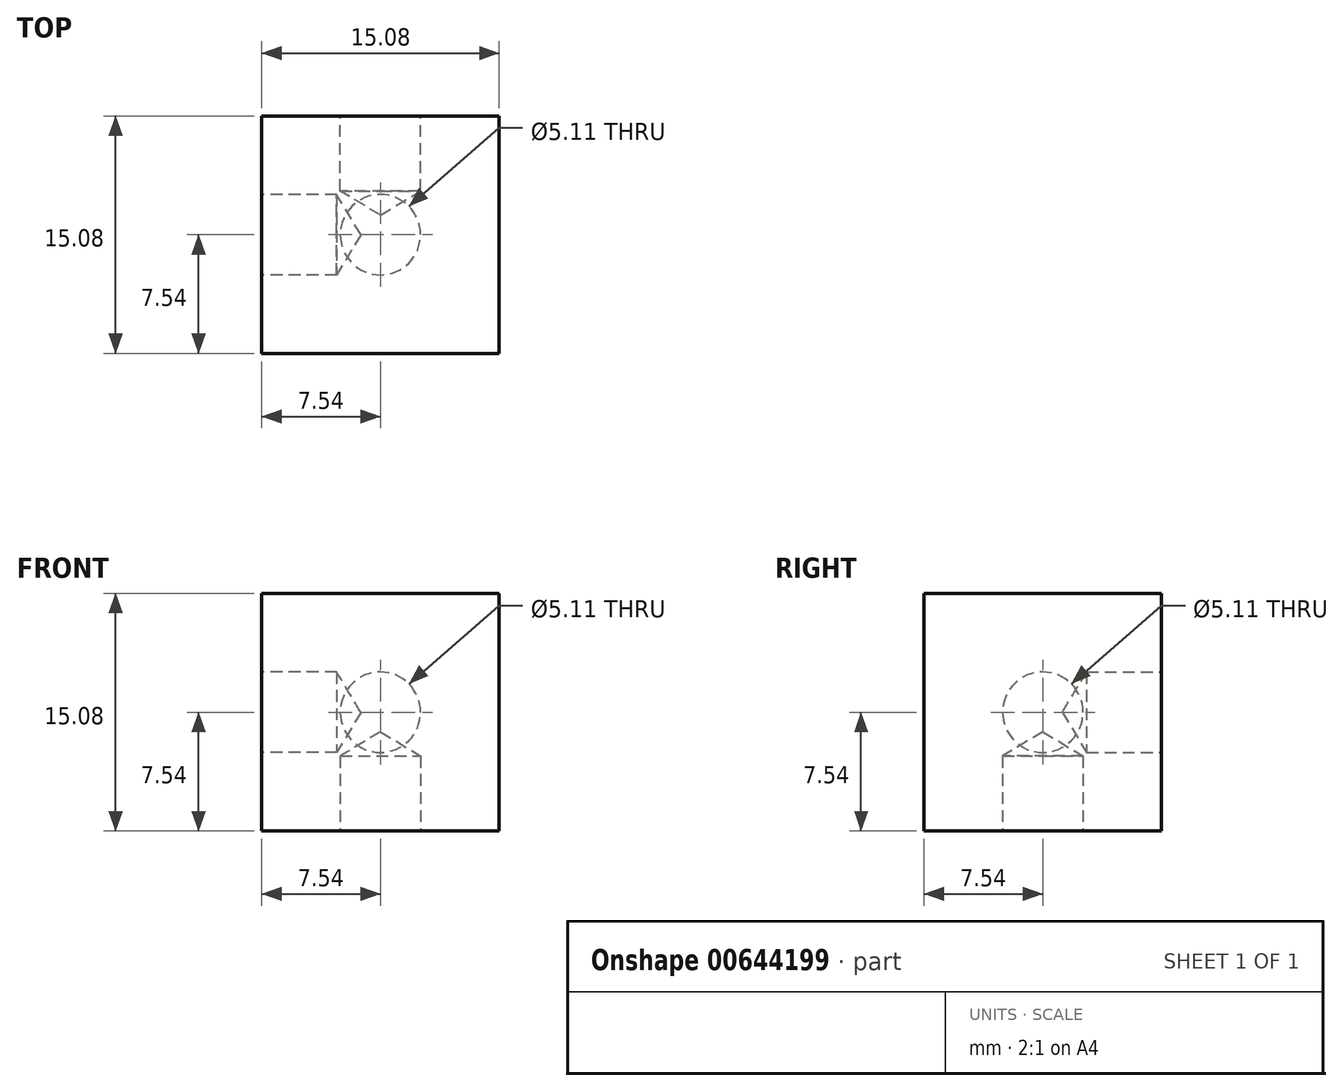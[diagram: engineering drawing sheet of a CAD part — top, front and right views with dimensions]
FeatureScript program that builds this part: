
annotation { "Feature Type Name" : "Feature", "Feature Type Description" : "" }
export const myFeature = defineFeature(function(context is Context, id is Id, definition is map)
    precondition{}
    {
        {
            var Q0;
            Q0=qCreatedBy(makeId("Top.planeOp"),FACE);
            var sketch = newSketch(context, id + "F0", { "sketchPlane" : qUnion([Q0])});
            skLineSegment(sketch, "E0.bottom", {"start": v(7.54, 7.54) * mm, "end": v(-7.54, 7.54) * mm});
            skLineSegment(sketch, "E0.top", {"start": v(7.54, -7.54) * mm, "end": v(-7.54, -7.54) * mm});
            skLineSegment(sketch, "E0.left", {"start": v(7.54, 7.54) * mm, "end": v(7.54, -7.54) * mm});
            skLineSegment(sketch, "E0.right", {"start": v(-7.54, 7.54) * mm, "end": v(-7.54, -7.54) * mm});
            skPoint(sketch, "E0.middle", {"position": v(0, 0) * mm});
            skSolve(sketch);
        }
        {
            var Q0;
            Q0=makeQuery(id+"F0.imprint","IMPRINT",FACE,{"disambiguationData":[TD([[makeQuery(id+"F0.imprint","IMPRINT",EDGE,{"derivedFrom":sQuery(id+"F0.wireOp",EDGE,"E0.bottom")}),1.0]])]});
            extrude(context, id + "F1", {"entities" : qUnion([Q0]), "endBound" : BoundingType.SYMMETRIC, "depth" : 15.08 * mm, "offsetDistance" : 25.4 * mm});
        }
        {
            var Q0;
            Q0=makeQuery(id+"F1.opExtrude","SWEPT_FACE",FACE,{"disambiguationData":[OSD([sQuery(id+"F0.wireOp",EDGE,"E0.right")])]});
            var sketch = newSketch(context, id + "F2", { "sketchPlane" : qUnion([Q0])});
            skPoint(sketch, "E1", {"position": v(0, 0) * mm});
            skSolve(sketch);
        }
        {
            var Q0;
            Q0=makeQuery(id+"F1.opExtrude","SWEPT_FACE",FACE,{"disambiguationData":[OSD([sQuery(id+"F0.wireOp",EDGE,"E0.bottom")])]});
            var sketch = newSketch(context, id + "F3", { "sketchPlane" : qUnion([Q0])});
            skPoint(sketch, "E2", {"position": v(0, 0) * mm});
            skSolve(sketch);
        }
        {
            var Q0;
            Q0=makeQuery(id+"F1.opExtrude","CAP_FACE",FACE,{"disambiguationData":[OSD([sQuery(id+"F0.wireOp",EDGE,"E0.bottom"),sQuery(id+"F0.wireOp",EDGE,"E0.top"),sQuery(id+"F0.wireOp",EDGE,"E0.left"),sQuery(id+"F0.wireOp",EDGE,"E0.right")])],"isStart":true});
            var sketch = newSketch(context, id + "F4", { "sketchPlane" : qUnion([Q0])});
            skPoint(sketch, "E3", {"position": v(0, 0) * mm});
            skSolve(sketch);
        }
        {
            var Q0;
            Q0=sQuery(id+"F4.wireOp",VERTEX,"E3");
            var Q1;
            Q1=makeQuery(id+"F1.opExtrude","SWEPT_BODY",BODY,{"disambiguationData":[OSD([sQuery(id+"F0.wireOp",EDGE,"E0.bottom"),sQuery(id+"F0.wireOp",EDGE,"E0.top"),sQuery(id+"F0.wireOp",EDGE,"E0.left"),sQuery(id+"F0.wireOp",EDGE,"E0.right")])]});
            hole(context, id + "F5", {"style" : HoleStyle.SIMPLE, "endStyle" : HoleEndStyle.BLIND, "standardTappedOrClearance" : lookupTablePath({ "standard" : "ANSI", "fit" : "Normal (ASME)", "size" : "#10", "type" : "Clearance" }), "standardBlindInLast" : lookupTablePath({ "fit" : "Free", "standard" : "ANSI", "size" : "#10", "type" : "Clearance" }), "holeDiameter" : 5.1 * mm, "majorDiameter" : 4.83 * mm, "holeDepth" : 4.76 * mm, "isTappedThrough" : true, "tappedDepth" : 12.7 * mm, "tapClearance" : 3, "locations" : qUnion([Q0]), "scope" : qUnion([Q1])});
        }
        {
            var Q0;
            Q0=sQuery(id+"F3.wireOp",VERTEX,"E2");
            var Q1;
            Q1=makeQuery(id+"F1.opExtrude","SWEPT_BODY",BODY,{"disambiguationData":[OSD([sQuery(id+"F0.wireOp",EDGE,"E0.bottom"),sQuery(id+"F0.wireOp",EDGE,"E0.top"),sQuery(id+"F0.wireOp",EDGE,"E0.left"),sQuery(id+"F0.wireOp",EDGE,"E0.right")])]});
            hole(context, id + "F6", {"style" : HoleStyle.SIMPLE, "endStyle" : HoleEndStyle.BLIND, "standardTappedOrClearance" : lookupTablePath({ "standard" : "ANSI", "fit" : "Normal (ASME)", "size" : "#10", "type" : "Clearance" }), "standardBlindInLast" : lookupTablePath({ "fit" : "Free", "standard" : "ANSI", "size" : "#10", "type" : "Clearance" }), "holeDiameter" : 5.1 * mm, "majorDiameter" : 6.35 * mm, "holeDepth" : 4.76 * mm, "isTappedThrough" : true, "tappedDepth" : 12.7 * mm, "tapClearance" : 3, "locations" : qUnion([Q0]), "scope" : qUnion([Q1])});
        }
        {
            var Q0;
            Q0=sQuery(id+"F2.wireOp",VERTEX,"E1");
            var Q1;
            Q1=makeQuery(id+"F1.opExtrude","SWEPT_BODY",BODY,{"disambiguationData":[OSD([sQuery(id+"F0.wireOp",EDGE,"E0.bottom"),sQuery(id+"F0.wireOp",EDGE,"E0.top"),sQuery(id+"F0.wireOp",EDGE,"E0.left"),sQuery(id+"F0.wireOp",EDGE,"E0.right")])]});
            hole(context, id + "F7", {"style" : HoleStyle.SIMPLE, "endStyle" : HoleEndStyle.BLIND, "standardTappedOrClearance" : lookupTablePath({ "standard" : "ANSI", "fit" : "Normal (ASME)", "size" : "#10", "type" : "Clearance" }), "standardBlindInLast" : lookupTablePath({ "fit" : "Free", "standard" : "ANSI", "size" : "#10", "type" : "Clearance" }), "holeDiameter" : 5.1 * mm, "majorDiameter" : 6.35 * mm, "holeDepth" : 4.76 * mm, "isTappedThrough" : true, "tappedDepth" : 12.7 * mm, "tapClearance" : 3, "locations" : qUnion([Q0]), "scope" : qUnion([Q1])});
        }
    });
